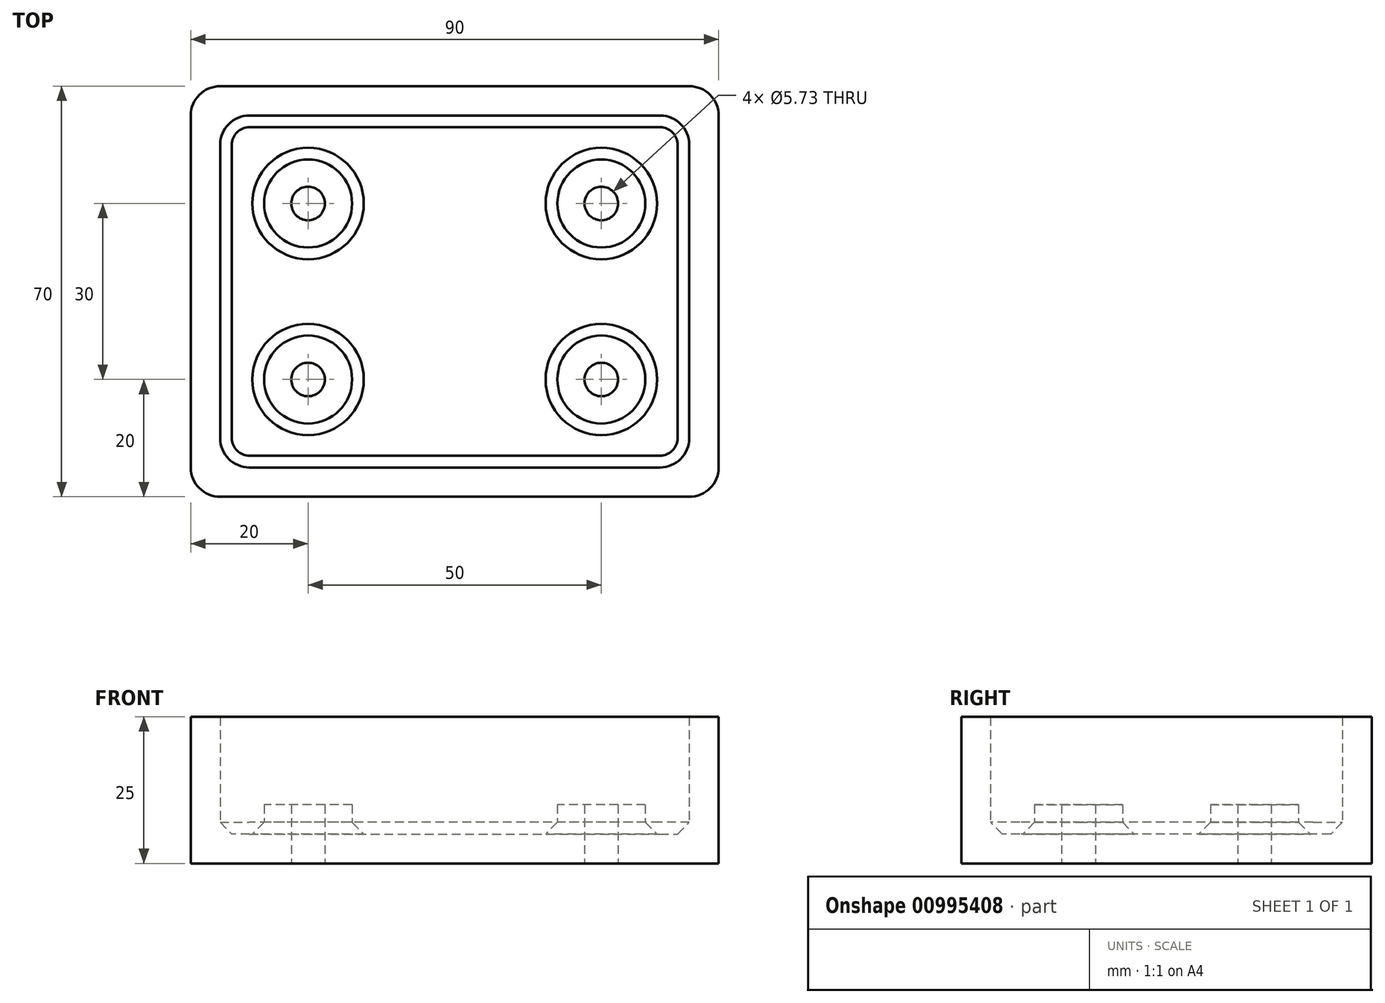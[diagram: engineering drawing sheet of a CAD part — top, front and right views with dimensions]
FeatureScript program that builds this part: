
annotation { "Feature Type Name" : "Feature", "Feature Type Description" : "" }
export const myFeature = defineFeature(function(context is Context, id is Id, definition is map)
    precondition{}
    {
        {
            var Q0;
            Q0=qCreatedBy(makeId("Top.planeOp"),FACE);
            var sketch = newSketch(context, id + "F0", { "sketchPlane" : qUnion([Q0])});
            skLineSegment(sketch, "E0.bottom", {"start": v(40, -30) * mm, "end": v(-40, -30) * mm});
            skLineSegment(sketch, "E0.top", {"start": v(40, 30) * mm, "end": v(-40, 30) * mm});
            skLineSegment(sketch, "E0.left", {"start": v(40, -30) * mm, "end": v(40, 30) * mm});
            skLineSegment(sketch, "E0.right", {"start": v(-40, -30) * mm, "end": v(-40, 30) * mm});
            skPoint(sketch, "E0.middle", {"position": v(0, 0) * mm});
            skLineSegment(sketch, "E1.0", {"start": v(45, 35) * mm, "end": v(-45, 35) * mm});
            skLineSegment(sketch, "E1.1", {"start": v(45, -35) * mm, "end": v(45, 35) * mm});
            skLineSegment(sketch, "E1.2", {"start": v(45, -35) * mm, "end": v(-45, -35) * mm});
            skLineSegment(sketch, "E1.3", {"start": v(-45, -35) * mm, "end": v(-45, 35) * mm});
            skLineSegment(sketch, "E2.0", {"start": v(25, -15) * mm, "end": v(25, 15) * mm, "construction": true});
            skLineSegment(sketch, "E2.1", {"start": v(-25, -15) * mm, "end": v(25, -15) * mm, "construction": true});
            skLineSegment(sketch, "E2.2", {"start": v(-25, 15) * mm, "end": v(-25, -15) * mm, "construction": true});
            skLineSegment(sketch, "E2.3", {"start": v(25, 15) * mm, "end": v(-25, 15) * mm, "construction": true});
            skCircle(sketch, "E3", {"center": v(-25, 15) * mm, "radius": 7.5 * mm});
            skCircle(sketch, "E4", {"center": v(25, 15) * mm, "radius": 7.5 * mm});
            skCircle(sketch, "E5", {"center": v(25, -15) * mm, "radius": 7.5 * mm});
            skCircle(sketch, "E6", {"center": v(-25, -15) * mm, "radius": 7.5 * mm});
            skCircle(sketch, "E7", {"center": v(-25, 15) * mm, "radius": 2.86 * mm});
            skCircle(sketch, "E8", {"center": v(25, 15) * mm, "radius": 2.86 * mm});
            skCircle(sketch, "E9", {"center": v(25, -15) * mm, "radius": 2.86 * mm});
            skCircle(sketch, "E10", {"center": v(-25, -15) * mm, "radius": 2.86 * mm});
            skSolve(sketch);
        }
        {
            var Q0;
            Q0=makeQuery(id+"F0.imprint","IMPRINT",FACE,{"disambiguationData":[TD([[makeQuery(id+"F0.imprint","IMPRINT",EDGE,{"derivedFrom":sQuery(id+"F0.wireOp",EDGE,"E0.bottom")}),1.0]])]});
            extrude(context, id + "F1", {"entities" : qUnion([Q0]), "depth" : 25 * mm, "offsetDistance" : 25 * mm});
        }
        {
            var Q0;
            Q0=makeQuery(id+"F0.imprint","IMPRINT",FACE,{"disambiguationData":[TD([[makeQuery(id+"F0.imprint","IMPRINT",EDGE,{"derivedFrom":sQuery(id+"F0.wireOp",EDGE,"E0.bottom")}),-1.0]])]});
            extrude(context, id + "F2", {"entities" : qUnion([Q0]), "operationType" : NewBodyOperationType.ADD, "depth" : 5 * mm, "offsetDistance" : 25 * mm});
        }
        {
            var Q0;
            Q0=makeQuery(id+"F0.imprint","IMPRINT",FACE,{"disambiguationData":[TD([[makeQuery(id+"F0.imprint","IMPRINT",EDGE,{"derivedFrom":sQuery(id+"F0.wireOp",EDGE,"E3")}),1.0]])]});
            var Q1;
            Q1=makeQuery(id+"F0.imprint","IMPRINT",FACE,{"disambiguationData":[TD([[makeQuery(id+"F0.imprint","IMPRINT",EDGE,{"derivedFrom":sQuery(id+"F0.wireOp",EDGE,"E6")}),1.0]])]});
            var Q2;
            Q2=makeQuery(id+"F0.imprint","IMPRINT",FACE,{"disambiguationData":[TD([[makeQuery(id+"F0.imprint","IMPRINT",EDGE,{"derivedFrom":sQuery(id+"F0.wireOp",EDGE,"E4")}),1.0]])]});
            var Q3;
            Q3=makeQuery(id+"F0.imprint","IMPRINT",FACE,{"disambiguationData":[TD([[makeQuery(id+"F0.imprint","IMPRINT",EDGE,{"derivedFrom":sQuery(id+"F0.wireOp",EDGE,"E5")}),1.0]])]});
            var Q4;
            Q4=makeQuery(id+"F2.opExtrude","CAP_FACE",FACE,{"disambiguationData":[OSD([sQuery(id+"F0.wireOp",EDGE,"E0.bottom"),sQuery(id+"F0.wireOp",EDGE,"E0.top"),sQuery(id+"F0.wireOp",EDGE,"E0.left"),sQuery(id+"F0.wireOp",EDGE,"E0.right"),sQuery(id+"F0.wireOp",EDGE,"E3"),sQuery(id+"F0.wireOp",EDGE,"E4"),sQuery(id+"F0.wireOp",EDGE,"E5"),sQuery(id+"F0.wireOp",EDGE,"E6")])],"isStart":false});
            extrude(context, id + "F3", {"entities" : qUnion([Q0, Q1, Q2, Q3]), "operationType" : NewBodyOperationType.ADD, "depth" : 10 * mm, "endBoundEntityFace" : qUnion([Q4]), "hasOffset" : true, "offsetDistance" : 5 * mm});
        }
        {
            var Q0;
            Q0=makeQuery(id+"F1.opExtrude","SWEPT_EDGE",EDGE,{"disambiguationData":[OSD([sQuery(id+"F0.wireOp",EDGE,"E0.top"),sQuery(id+"F0.wireOp",EDGE,"E0.right")])]});
            var Q1;
            Q1=makeQuery(id+"F1.opExtrude","SWEPT_EDGE",EDGE,{"disambiguationData":[OSD([sQuery(id+"F0.wireOp",EDGE,"E1.0"),sQuery(id+"F0.wireOp",EDGE,"E1.1")])]});
            var Q2;
            Q2=makeQuery(id+"F1.opExtrude","SWEPT_EDGE",EDGE,{"disambiguationData":[OSD([sQuery(id+"F0.wireOp",EDGE,"E1.1"),sQuery(id+"F0.wireOp",EDGE,"E1.2")])]});
            var Q3;
            Q3=makeQuery(id+"F1.opExtrude","SWEPT_EDGE",EDGE,{"disambiguationData":[OSD([sQuery(id+"F0.wireOp",EDGE,"E1.2"),sQuery(id+"F0.wireOp",EDGE,"E1.3")])]});
            var Q4;
            Q4=makeQuery(id+"F1.opExtrude","SWEPT_EDGE",EDGE,{"disambiguationData":[OSD([sQuery(id+"F0.wireOp",EDGE,"E1.0"),sQuery(id+"F0.wireOp",EDGE,"E1.3")])]});
            var Q5;
            Q5=makeQuery(id+"F1.opExtrude","SWEPT_EDGE",EDGE,{"disambiguationData":[OSD([sQuery(id+"F0.wireOp",EDGE,"E0.bottom"),sQuery(id+"F0.wireOp",EDGE,"E0.left")])]});
            var Q6;
            Q6=makeQuery(id+"F1.opExtrude","SWEPT_EDGE",EDGE,{"disambiguationData":[OSD([sQuery(id+"F0.wireOp",EDGE,"E0.bottom"),sQuery(id+"F0.wireOp",EDGE,"E0.right")])]});
            var Q7;
            Q7=makeQuery(id+"F1.opExtrude","SWEPT_EDGE",EDGE,{"disambiguationData":[OSD([sQuery(id+"F0.wireOp",EDGE,"E0.top"),sQuery(id+"F0.wireOp",EDGE,"E0.left")])]});
            fillet(context, id + "F4", {"entities" : qUnion([Q0, Q1, Q2, Q3, Q4, Q5, Q6, Q7]), "radius" : 5 * mm, "tangentPropagation" : true, "allowEdgeOverflow" : false});
        }
        {
            var Q0;
            Q0=makeQuery(id+"F2.opExtrude","CAP_EDGE",EDGE,{"disambiguationData":[OSD([sQuery(id+"F0.wireOp",EDGE,"E3")])],"isStart":false});
            var Q1;
            Q1=makeQuery(id+"F2.opExtrude","CAP_EDGE",EDGE,{"disambiguationData":[OSD([sQuery(id+"F0.wireOp",EDGE,"E4")])],"isStart":false});
            var Q2;
            Q2=makeQuery(id+"F2.opExtrude","CAP_EDGE",EDGE,{"disambiguationData":[OSD([sQuery(id+"F0.wireOp",EDGE,"E6")])],"isStart":false});
            var Q3;
            Q3=makeQuery(id+"F2.opExtrude","CAP_FACE",FACE,{"disambiguationData":[OSD([sQuery(id+"F0.wireOp",EDGE,"E0.bottom"),sQuery(id+"F0.wireOp",EDGE,"E0.top"),sQuery(id+"F0.wireOp",EDGE,"E0.left"),sQuery(id+"F0.wireOp",EDGE,"E0.right"),sQuery(id+"F0.wireOp",EDGE,"E3"),sQuery(id+"F0.wireOp",EDGE,"E4"),sQuery(id+"F0.wireOp",EDGE,"E5"),sQuery(id+"F0.wireOp",EDGE,"E6")])],"isStart":false});
            chamfer(context, id + "F5", {"entities" : qUnion([Q0, Q1, Q2, Q3]), "width" : 2 * mm, "tangentPropagation" : true});
        }
    });
